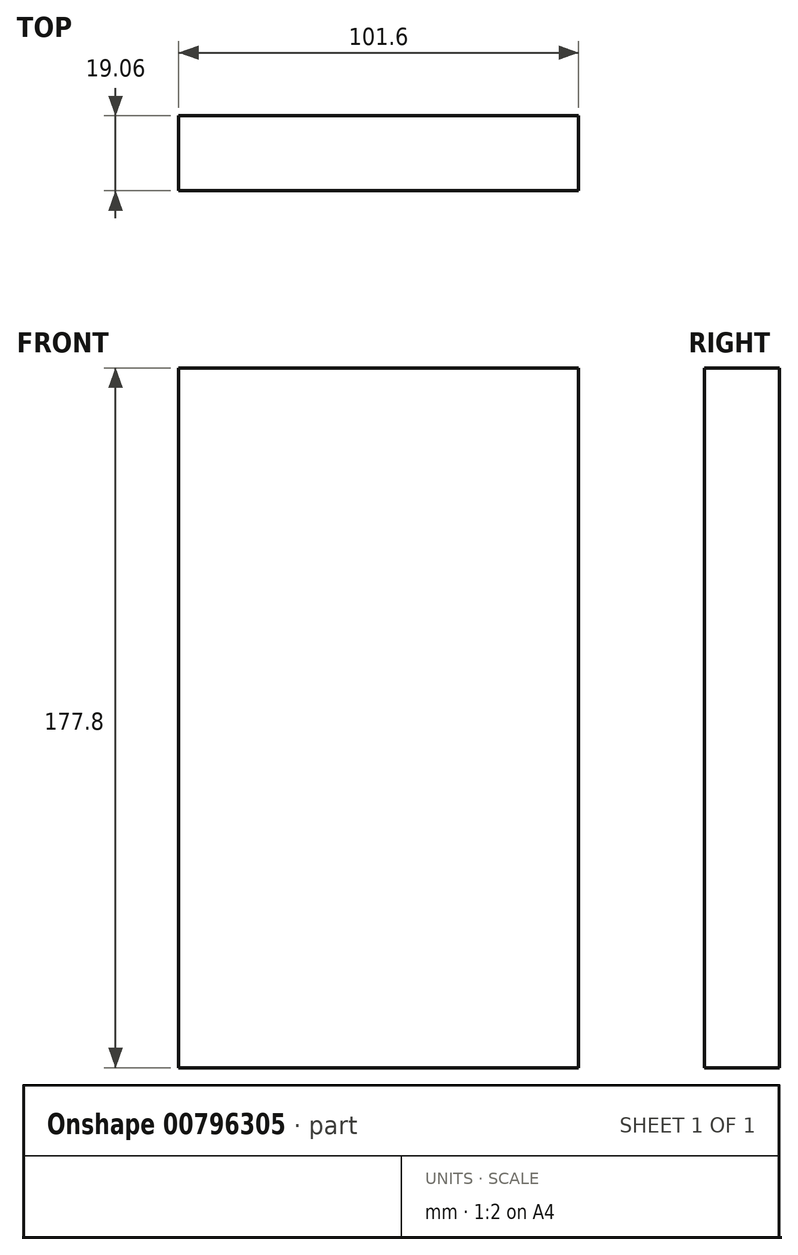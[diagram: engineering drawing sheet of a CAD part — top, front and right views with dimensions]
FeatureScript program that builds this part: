
annotation { "Feature Type Name" : "Feature", "Feature Type Description" : "" }
export const myFeature = defineFeature(function(context is Context, id is Id, definition is map)
    precondition{}
    {
        {
            var Q0;
            Q0=qCreatedBy(makeId("Front.planeOp"),FACE);
            var sketch = newSketch(context, id + "F0", { "sketchPlane" : qUnion([Q0])});
            skLineSegment(sketch, "E0.bottom", {"start": v(-50.8, 88.9) * mm, "end": v(50.8, 88.9) * mm});
            skLineSegment(sketch, "E0.top", {"start": v(-50.8, -88.9) * mm, "end": v(50.8, -88.9) * mm});
            skLineSegment(sketch, "E0.left", {"start": v(-50.8, 88.9) * mm, "end": v(-50.8, -88.9) * mm});
            skLineSegment(sketch, "E0.right", {"start": v(50.8, 88.9) * mm, "end": v(50.8, -88.9) * mm});
            skPoint(sketch, "E0.middle", {"position": v(0, 0) * mm});
            skSolve(sketch);
        }
        {
            var Q0;
            Q0 = qSketchRegion(id + "F0", true);
            extrude(context, id + "F1", {"entities" : qUnion([Q0]), "endBound" : BoundingType.SYMMETRIC, "depth" : 19.05 * mm, "offsetDistance" : 25.4 * mm});
        }
    });
